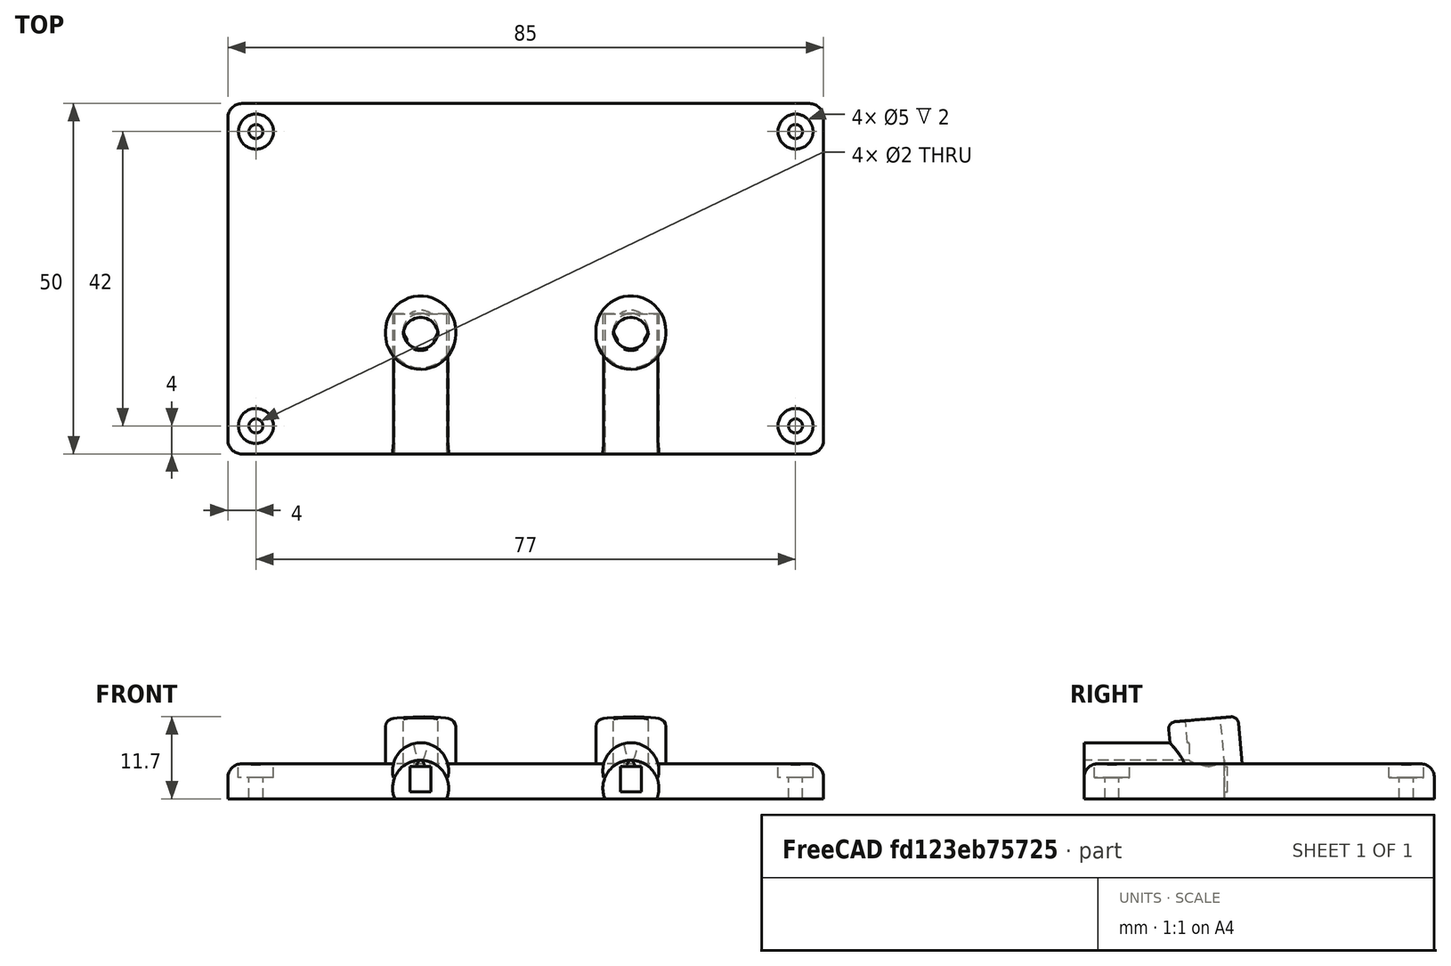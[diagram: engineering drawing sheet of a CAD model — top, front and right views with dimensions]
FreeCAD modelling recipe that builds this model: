
FCSTD DOCUMENT  (FreeCAD 0.19R24276 (Git))
Label: enclosureBase2
License: All rights reserved
LicenseURL: http://en.wikipedia.org/wiki/All_rights_reserved
objects: Part::Cylinder×14, Part::MultiFuse×8, Part::Fillet×3, Part::FeaturePython×2, Part::Cut×2, Spreadsheet::Sheet×1, Part::Box×1
note: 30 computed .brp shape members not serialized (recipe doc carries the construction recipe); baked Part::Feature solids carry a one-line shape summary decoded from their .brp

FEATURE [Spreadsheet::Sheet] Spreadsheet  label="data"
  cells = A4=hole_dia; B4(hole_dia)==1mm; A5=standoff_dia; B5(standoff_dia)==4mm; A6=standoff_height; B6(standoff_height)==8mm; A7=case_standoff_dia; B7(case_standoff_dia)==5mm; A8=wall_thickness; B8(wall_thickness)==5mm; A9=case_thickness; B9(case_thickness)==15mm; A10=case_inner_width; B10(case_inner_width)==85mm; A11=case_inner_height; B11(case_inner_height)==50mm; A12=post_dia; B12(post_dia)==5mm; A13=post_depth; B13(post_depth)==10mm; A14=offset; B14(offset)==4mm; A15=screwHeadDia; B15(screwHeadDia)==5mm
FEATURE [Part::Box] Box  label="Cube"
  AttacherType = Attacher::AttachEngine3D
  Height = 5
  Length = 85
  Placement = pos=(-42.5,-25,0) rot=(0,0,1;0rad)
  Width = 50
  expr: Length = <<data>>.case_inner_width
  expr: Width = <<data>>.case_inner_height
  expr: .Placement.Base.y = -<<data>>.case_inner_height / 2
  expr: .Placement.Base.x = -<<data>>.case_inner_width / 2
  expr: Height = <<data>>.wall_thickness
FEATURE [Part::Cylinder] Cylinder
  Angle = 360
  AttacherType = Attacher::AttachEngine3D
  Height = 2
  Placement = pos=(0,0,3) rot=(0,0,1;0rad)
  Radius = 2.5
  expr: .Placement.Base.z = <<data>>.wall_thickness - 2mm
  expr: Radius = <<data>>.screwHeadDia / 2
FEATURE [Part::Cylinder] Cylinder001
  Angle = 360
  AttacherType = Attacher::AttachEngine3D
  Height = 10
  Radius = 1
FEATURE [Part::MultiFuse] Fusion  label="screwHole"
  Placement = pos=(38.5,21,0) rot=(0,0,1;0rad)
  Shapes = -> [Cylinder001,Cylinder]
  expr: .Placement.Base.x = <<data>>.case_inner_width / 2 - <<data>>.offset
  expr: .Placement.Base.y = <<data>>.case_inner_height / 2 - <<data>>.offset
FEATURE [Part::Cylinder] Cylinder002
  Angle = 360
  AttacherType = Attacher::AttachEngine3D
  Height = 2
  Placement = pos=(0,0,3) rot=(0,0,1;0rad)
  Radius = 2.5
  expr: .Placement.Base.z = <<data>>.wall_thickness - 2mm
  expr: Radius = <<data>>.screwHeadDia / 2
FEATURE [Part::Cylinder] Cylinder003
  Angle = 360
  AttacherType = Attacher::AttachEngine3D
  Height = 10
  Radius = 1
FEATURE [Part::MultiFuse] Fusion006  label="screwHole001"
  Placement = pos=(-38.5,21,0) rot=(0,0,1;0rad)
  Shapes = -> [Cylinder003,Cylinder002]
  expr: .Placement.Base.x = -<<data>>.case_inner_width / 2 + <<data>>.offset
  expr: .Placement.Base.y = <<data>>.case_inner_height / 2 - <<data>>.offset
FEATURE [Part::Cylinder] Cylinder004
  Angle = 360
  AttacherType = Attacher::AttachEngine3D
  Height = 2
  Placement = pos=(0,0,3) rot=(0,0,1;0rad)
  Radius = 2.5
  expr: .Placement.Base.z = <<data>>.wall_thickness - 2mm
  expr: Radius = <<data>>.screwHeadDia / 2
FEATURE [Part::Cylinder] Cylinder005
  Angle = 360
  AttacherType = Attacher::AttachEngine3D
  Height = 10
  Radius = 1
FEATURE [Part::MultiFuse] Fusion007  label="screwHole002"
  Placement = pos=(38.5,-21,0) rot=(0,0,1;0rad)
  Shapes = -> [Cylinder005,Cylinder004]
  expr: .Placement.Base.x = <<data>>.case_inner_width / 2 - <<data>>.offset
  expr: .Placement.Base.y = -<<data>>.case_inner_height / 2 + <<data>>.offset
FEATURE [Part::Cylinder] Cylinder006
  Angle = 360
  AttacherType = Attacher::AttachEngine3D
  Height = 2
  Placement = pos=(0,0,3) rot=(0,0,1;0rad)
  Radius = 2.5
  expr: Radius = <<data>>.screwHeadDia / 2
  expr: .Placement.Base.z = <<data>>.wall_thickness - 2mm
FEATURE [Part::Cylinder] Cylinder007
  Angle = 360
  AttacherType = Attacher::AttachEngine3D
  Height = 10
  Radius = 1
FEATURE [Part::MultiFuse] Fusion008  label="screwHole003"
  Placement = pos=(-38.5,-21,0) rot=(0,0,1;0rad)
  Shapes = -> [Cylinder007,Cylinder006]
  expr: .Placement.Base.x = -<<data>>.case_inner_width / 2 + <<data>>.offset
  expr: .Placement.Base.y = -<<data>>.case_inner_height / 2 + <<data>>.offset
FEATURE [Part::FeaturePython] Tube  # WARN: FeaturePython — macro-defined, semantics opaque (R4)
  AttacherType = Attacher::AttachEngine3D
  Height = 7
  InnerRadius = 2.5
  OuterRadius = 5
  Placement = pos=(-15,-7,5) rot=(0,0,1;0rad)
  expr: OuterRadius = <<data>>.post_dia / 2 + <<data>>.wall_thickness / 2
  expr: .Placement.Base.z = <<data>>.wall_thickness
FEATURE [Part::FeaturePython] Tube001  # WARN: FeaturePython — macro-defined, semantics opaque (R4)
  AttacherType = Attacher::AttachEngine3D
  Height = 7
  InnerRadius = 2.5
  OuterRadius = 5
  Placement = pos=(15,-7,5) rot=(0,0,1;0rad)
  expr: OuterRadius = <<data>>.post_dia / 2 + <<data>>.wall_thickness / 2
  expr: .Placement.Base.z = <<data>>.wall_thickness
FEATURE [Part::Cylinder] Cylinder008
  Angle = 360
  AttacherType = Attacher::AttachEngine3D
  Height = 10
  Placement = pos=(-15,-7,1) rot=(0,0,1;0rad)
  Radius = 2.5
  expr: Radius = <<data>>.post_dia / 2
FEATURE [Part::Cylinder] Cylinder009
  Angle = 360
  AttacherType = Attacher::AttachEngine3D
  Height = 10
  Placement = pos=(15,-7,1) rot=(0,0,1;0rad)
  Radius = 2.5
  expr: Radius = <<data>>.post_dia / 2
FEATURE [Part::MultiFuse] Fusion009  label="holes"
  Shapes = -> [Cylinder009,Cylinder008,Fusion008,Fusion007,Fusion006,Fusion]
FEATURE [Part::Fillet] Fillet
  Base = -> Box
  Edges = 8 edges r=2: [Edge1,Edge2,Edge3,Edge5,Edge6,Edge7,Edge10,Edge12]
FEATURE [Part::Fillet] Fillet001
  Base = -> Tube
  Edges = 1 edges r=1: [Edge1]
FEATURE [Part::Fillet] Fillet002
  Base = -> Tube001
  Edges = 1 edges r=1: [Edge1]
FEATURE [Part::Cylinder] Cylinder010
  Angle = 360
  AttacherType = Attacher::AttachEngine3D
  Height = 30
  Placement = pos=(-15,-5,0) rot=(1,0,0;1.5708rad)
  Radius = 4
FEATURE [Part::Cylinder] Cylinder011
  Angle = 360
  AttacherType = Attacher::AttachEngine3D
  Height = 30
  Placement = pos=(15,-5,0) rot=(1,0,0;1.5708rad)
  Radius = 4
FEATURE [Part::Cut] Cut
  Base = -> Fillet
  Tool = -> Fusion009
FEATURE [Part::MultiFuse] Fusion010
  Placement = pos=(0,0,1.5) rot=(0,0,1;0rad)
  Shapes = -> [Cylinder011,Cylinder010]
FEATURE [Part::MultiFuse] Fusion012
  Placement = pos=(0,0,0) rot=(1,0,0;0.087266rad)
  Shapes = -> [Fillet002,Fillet001]
FEATURE [Part::Cylinder] Cylinder012
  Angle = 360
  AttacherType = Attacher::AttachEngine3D
  Height = 15
  Placement = pos=(15,-10,4) rot=(1,0,0;1.5708rad)
  Radius = 4
FEATURE [Part::Cylinder] Cylinder013
  Angle = 360
  AttacherType = Attacher::AttachEngine3D
  Height = 15
  Placement = pos=(-15,-10,4) rot=(1,0,0;1.5708rad)
  Radius = 4
FEATURE [Part::MultiFuse] Fusion013
  Shapes = -> [Cut,Fusion012,Cylinder012,Cylinder013]
FEATURE [Part::Cut] Cut001  label="DisplayBase"
  Base = -> Fusion013
  Tool = -> Fusion010
